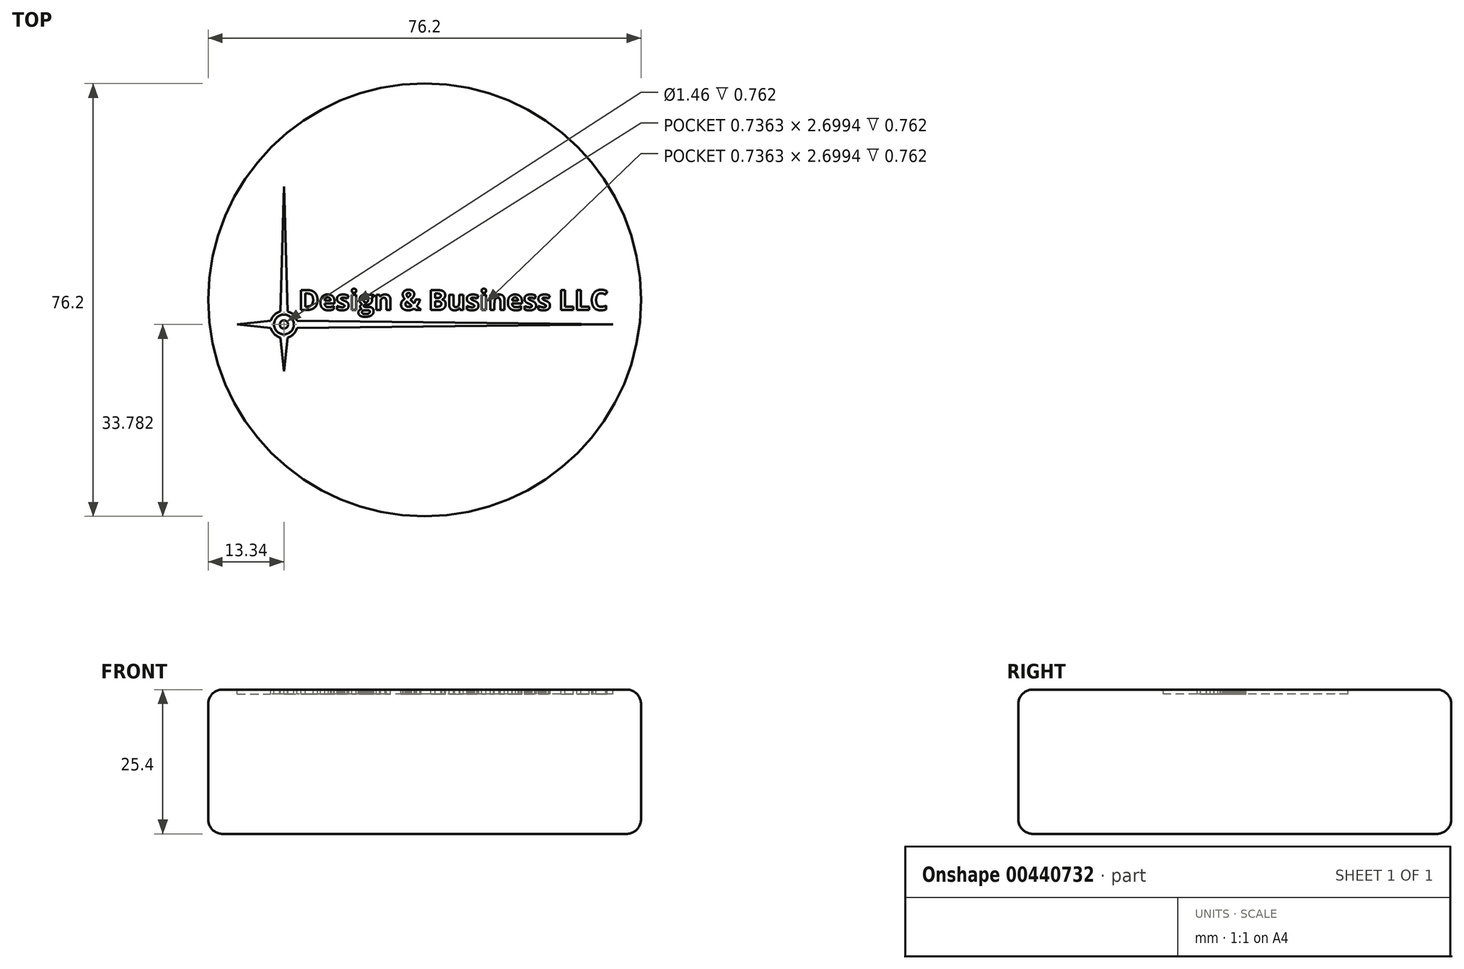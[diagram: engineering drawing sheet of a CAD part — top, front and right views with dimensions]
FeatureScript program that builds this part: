
annotation { "Feature Type Name" : "Feature", "Feature Type Description" : "" }
export const myFeature = defineFeature(function(context is Context, id is Id, definition is map)
    precondition{}
    {
        {
            var Q0;
            Q0=qCreatedBy(makeId("Front.planeOp"),FACE);
            var sketch = newSketch(context, id + "F0", { "sketchPlane" : qUnion([Q0])});
            skLineSegment(sketch, "E0", {"start": v(0, 0) * mm, "end": v(35.56, 0) * mm});
            skLineSegment(sketch, "E1", {"start": v(38.1, 2.54) * mm, "end": v(38.1, 22.86) * mm});
            skLineSegment(sketch, "E2", {"start": v(35.56, 25.4) * mm, "end": v(0, 25.4) * mm});
            skLineSegment(sketch, "E3", {"start": v(0, 25.4) * mm, "end": v(0, 0) * mm});
            skPoint(sketch, "E4.visualSharp", {"position": v(38.1, 0) * mm});
            skArc(sketch, "E4.filletArc", {"start": v(35.56, 0) * mm, "mid": v(37.36, 0.74) * mm, "end": v(38.1, 2.54) * mm});
            skPoint(sketch, "E5.visualSharp", {"position": v(38.1, 25.4) * mm});
            skArc(sketch, "E5.filletArc", {"start": v(38.1, 22.86) * mm, "mid": v(37.36, 24.66) * mm, "end": v(35.56, 25.4) * mm});
            skSolve(sketch);
        }
        {
            var Q0;
            Q0=makeQuery(id+"F0.imprint","IMPRINT",FACE,{"disambiguationData":[TD([[makeQuery(id+"F0.imprint","IMPRINT",EDGE,{"derivedFrom":sQuery(id+"F0.wireOp",EDGE,"E0")}),1.0]])]});
            var Q1;
            Q1 = qConstructionFilter(qBodyType(qCreatedBy(id + "F0" ,EDGE), BodyType.WIRE), ConstructionObject.NO);
            var Q2;
            Q2=sQuery(id+"F0.wireOp",EDGE,"E3");
            revolve(context, id + "F1", {"entities" : qUnion([Q0]), "surfaceEntities" : qUnion([Q1]), "axis" : qUnion([Q2]), "revolveType" : RevolveType.FULL});
        }
        {
            var Q0;
            Q0=makeQuery(id+"F1.opRevolve","SWEPT_FACE",FACE,{"disambiguationData":[OSD([sQuery(id+"F0.wireOp",EDGE,"E2")])]});
            var sketch = newSketch(context, id + "F2", { "sketchPlane" : qUnion([Q0])});
            skText(sketch, "E6", { "text": "Design & Business LLC", "fontName": "OpenSans-Bold.ttf"});
            skPoint(sketch, "E7", {"position": v(2.54, 0) * mm});
            skPoint(sketch, "E8", {"position": v(-35.56, 0) * mm});
            skCircle(sketch, "E9", {"center": v(-24.76, -4.32) * mm, "radius": 2.4 * mm});
            skCircle(sketch, "E10", {"center": v(-24.76, -4.32) * mm, "radius": 1.74 * mm});
            skCircle(sketch, "E11", {"center": v(-24.76, -4.32) * mm, "radius": 0.73 * mm});
            skLineSegment(sketch, "E12", {"start": v(-24.76, -4.32) * mm, "end": v(-24.76, 19.94) * mm, "construction": true});
            skLineSegment(sketch, "E13", {"start": v(-24.76, -4.32) * mm, "end": v(33.17, -4.32) * mm, "construction": true});
            skLineSegment(sketch, "E14", {"start": v(-24.76, 19.94) * mm, "end": v(-25.4, -2.01) * mm});
            skLineSegment(sketch, "E15", {"start": v(-25.4, -2.01) * mm, "end": v(-24.76, -2.01) * mm});
            skLineSegment(sketch, "E16", {"start": v(33.17, -4.32) * mm, "end": v(-22.46, -4.95) * mm});
            skLineSegment(sketch, "E17", {"start": v(-22.46, -4.95) * mm, "end": v(-22.46, -4.32) * mm});
            skLineSegment(sketch, "E18.MirrorCS", {"start": v(33.17, -4.32) * mm, "end": v(-22.46, -3.68) * mm});
            skLineSegment(sketch, "E19.MirrorCS", {"start": v(-24.76, 19.94) * mm, "end": v(-24.13, -2.01) * mm});
            skLineSegment(sketch, "E20", {"start": v(-25.4, -6.62) * mm, "end": v(-24.76, -12.57) * mm});
            skLineSegment(sketch, "E21", {"start": v(-24.76, -12.57) * mm, "end": v(-24.13, -6.62) * mm});
            skLineSegment(sketch, "E22", {"start": v(-27.06, -4.95) * mm, "end": v(-33.02, -4.32) * mm});
            skLineSegment(sketch, "E23", {"start": v(-33.02, -4.32) * mm, "end": v(-27.06, -3.68) * mm});
            const initialGuessF2  = {"E6": [-0.02222, -0.00178, 1, 0, 0.00356]};
            skSetInitialGuess(sketch, initialGuessF2);
            skSolve(sketch);
        }
        {
            var Q0;
            Q0 = qSketchRegion(id + "F2", true);
            var Q1;
            Q1=makeQuery(id+"F2.imprint","IMPRINT",FACE,{"disambiguationData":[TD([[makeQuery(id+"F2.imprint","IMPRINT",EDGE,{"derivedFrom":sQuery(id+"F2.wireOp",EDGE,"E11")}),1.0]])]});
            extrude(context, id + "F3", {"entities" : qUnion([Q0, Q1]), "operationType" : NewBodyOperationType.REMOVE, "oppositeDirection" : true, "depth" : 0.76 * mm});
        }
    });
